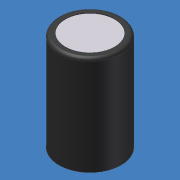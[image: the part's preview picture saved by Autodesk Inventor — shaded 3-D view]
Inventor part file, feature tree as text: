
AUTODESK INVENTOR PART (.ipt)
format: ipt  version: 2014 SP1 (Build 180222100, 222)  size: 111,616 bytes
history: native  units: mm (DEFAULTED — no unit token found)
features: extrude x2, sketch x2, fillet x1
ambient origin geometry x8: Origin, YZ Plane, XZ Plane, XY Plane, X Axis, Y Axis, Z Axis, Center Point
bodies: Solid1 (feature_tree)
feature tree (5):
  extrude  "Extrusion1"  Depth=20.32mm TaperAngle=0.0deg
  fillet  "Fillet1"  Radius=0.635mm
  extrude  "Extrusion2"  [1 undecoded]
  sketch  "Sketch1"  dims[d0=12.7mm d1=20.32mm d2=0.0mm d3=0.635mm]
  sketch  "Sketch2"  dims[d4=0.127mm d5=0.0mm]
note: 1 required parameter value undecoded (feature->parameter linkage not recoverable at this tier; creation-order binding heuristic only, values carry confidence <= 0.55)
